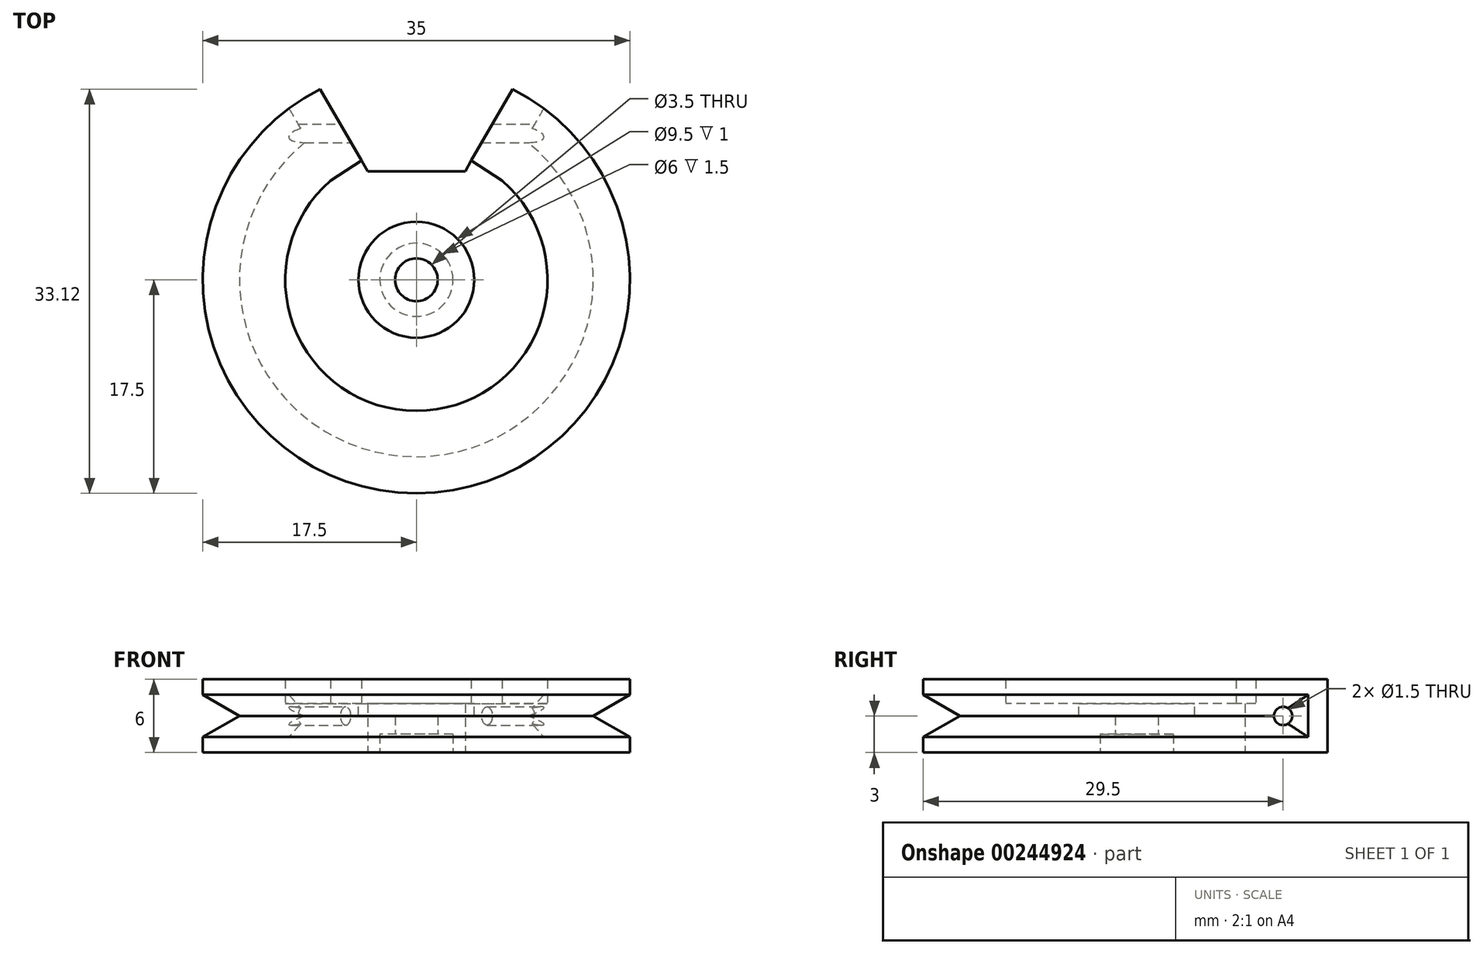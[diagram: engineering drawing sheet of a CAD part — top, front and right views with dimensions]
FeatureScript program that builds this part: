
annotation { "Feature Type Name" : "Feature", "Feature Type Description" : "" }
export const myFeature = defineFeature(function(context is Context, id is Id, definition is map)
    precondition{}
    {
        {
            var Q0;
            Q0=qCreatedBy(makeId("Top.planeOp"),FACE);
            var sketch = newSketch(context, id + "F0", { "sketchPlane" : qUnion([Q0])});
            skCircle(sketch, "E0", {"center": v(0, 0) * mm, "radius": 10.75 * mm});
            skCircle(sketch, "E1", {"center": v(0, 0) * mm, "radius": 17.5 * mm});
            skSolve(sketch);
        }
        {
            var Q0;
            Q0 = qSketchRegion(id + "F0", true);
            extrude(context, id + "F1", {"entities" : qUnion([Q0]), "depth" : 6 * mm});
        }
        {
            var Q0;
            Q0=qCreatedBy(makeId("Top.planeOp"),FACE);
            var sketch = newSketch(context, id + "F2", { "sketchPlane" : qUnion([Q0])});
            skCircle(sketch, "E2", {"center": v(0, 0) * mm, "radius": 10.75 * mm});
            skCircle(sketch, "E3", {"center": v(0, 0) * mm, "radius": 1.75 * mm});
            skSolve(sketch);
        }
        {
            var Q0;
            Q0 = qSketchRegion(id + "F2", true);
            extrude(context, id + "F3", {"entities" : qUnion([Q0]), "operationType" : NewBodyOperationType.ADD, "depth" : 4 * mm});
        }
        {
            var Q0;
            Q0=qCreatedBy(makeId("Front.planeOp"),FACE);
            var sketch = newSketch(context, id + "F4", { "sketchPlane" : qUnion([Q0])});
            skLineSegment(sketch, "E4", {"start": v(0, 0) * mm, "end": v(14.5, 0) * mm});
            skLineSegment(sketch, "E5", {"start": v(14.5, 0) * mm, "end": v(14.5, 3) * mm});
            skLineSegment(sketch, "E6", {"start": v(14.5, 3) * mm, "end": v(17.53, 4.75) * mm});
            skLineSegment(sketch, "E7", {"start": v(14.5, 3) * mm, "end": v(17.53, 1.25) * mm});
            skLineSegment(sketch, "E8", {"start": v(17.53, 1.25) * mm, "end": v(17.53, 4.75) * mm});
            skSolve(sketch);
        }
        {
            var Q0;
            Q0 = qSketchRegion(id + "F4", true);
            var Q1;
            Q1=makeQuery(id+"F1.opExtrude","CAP_EDGE",EDGE,{"disambiguationData":[OSD([sQuery(id+"F0.wireOp",EDGE,"E1")])],"isStart":false});
            sweep(context, id + "F5", {"operationType" : NewBodyOperationType.REMOVE, "profiles" : qUnion([Q0]), "path" : qUnion([Q1])});
        }
        {
            var Q0;
            Q0=qCreatedBy(makeId("Top.planeOp"),FACE);
            var sketch = newSketch(context, id + "F6", { "sketchPlane" : qUnion([Q0])});
            skArc(sketch, "E9", {"start": v(4, 8.9) * mm, "mid": v(0, 9.75) * mm, "end": v(-4, 8.9) * mm});
            skLineSegment(sketch, "E10", {"start": v(4, 8.9) * mm, "end": v(9.5, 18.42) * mm});
            skLineSegment(sketch, "E11", {"start": v(-4, 8.9) * mm, "end": v(-9.5, 18.42) * mm});
            skLineSegment(sketch, "E12", {"start": v(-9.5, 18.42) * mm, "end": v(9.5, 18.42) * mm});
            skLineSegment(sketch, "E13", {"start": v(-4, 8.9) * mm, "end": v(4, 8.9) * mm});
            skSolve(sketch);
        }
        {
            var Q0;
            Q0=qCreatedBy(makeId("Top.planeOp"),FACE);
            var sketch = newSketch(context, id + "F7", { "sketchPlane" : qUnion([Q0])});
            skArc(sketch, "E14", {"start": v(-7.89, 15.62) * mm, "mid": v(-9.2, 14.89) * mm, "end": v(-10.44, 14.05) * mm});
            skArc(sketch, "E15", {"start": v(7.03, 8.14) * mm, "mid": v(0, 10.75) * mm, "end": v(-7.03, 8.14) * mm});
            skLineSegment(sketch, "E16", {"start": v(-4.5, 9.76) * mm, "end": v(-7.89, 15.62) * mm});
            skLineSegment(sketch, "E17", {"start": v(4.5, 9.76) * mm, "end": v(7.89, 15.62) * mm});
            skLineSegment(sketch, "E18", {"start": v(-7.03, 8.14) * mm, "end": v(-10.44, 14.05) * mm});
            skLineSegment(sketch, "E19", {"start": v(7.03, 8.14) * mm, "end": v(10.44, 14.05) * mm});
            skLineSegment(sketch, "E20", {"start": v(5.94, 12.26) * mm, "end": v(8.54, 10.76) * mm});
            skLineSegment(sketch, "E21", {"start": v(-5.94, 12.26) * mm, "end": v(-8.54, 10.76) * mm});
            skLineSegment(sketch, "E22", {"start": v(7.03, 8.14) * mm, "end": v(4.5, 9.76) * mm});
            skPoint(sketch, "E23.orphan", {"position": v(4, 8.9) * mm});
            skLineSegment(sketch, "E24", {"start": v(-7.03, 8.14) * mm, "end": v(-4.5, 9.76) * mm});
            skPoint(sketch, "E25.orphan", {"position": v(-4, 8.9) * mm});
            skArc(sketch, "E26.trimOffspring", {"start": v(10.44, 14.05) * mm, "mid": v(9.2, 14.89) * mm, "end": v(7.89, 15.62) * mm});
            skSolve(sketch);
        }
        {
            var Q0;
            Q0 = qSketchRegion(id + "F6", true);
            extrude(context, id + "F8", {"entities" : qUnion([Q0]), "operationType" : NewBodyOperationType.REMOVE, "depth" : 6 * mm});
        }
        {
            var Q0;
            Q0 = qSketchRegion(id + "F7", true);
            extrude(context, id + "F9", {"entities" : qUnion([Q0]), "operationType" : NewBodyOperationType.ADD, "depth" : 6 * mm});
        }
        {
            var Q0;
            Q0=qCreatedBy(makeId("Right.planeOp"),FACE);
            var sketch = newSketch(context, id + "F10", { "sketchPlane" : qUnion([Q0])});
            skLineSegment(sketch, "E27", {"start": v(0, 0) * mm, "end": v(12, 0) * mm});
            skLineSegment(sketch, "E28", {"start": v(12, 0) * mm, "end": v(12, 3) * mm});
            skCircle(sketch, "E29", {"center": v(12, 3) * mm, "radius": 0.75 * mm});
            skSolve(sketch);
        }
        {
            var Q0;
            Q0=makeQuery(id+"F10.imprint","IMPRINT",FACE,{"disambiguationData":[TD([[makeQuery(id+"F10.imprint","IMPRINT",EDGE,{"derivedFrom":sQuery(id+"F10.wireOp",EDGE,"E29")}),1.0]])]});
            extrude(context, id + "F11", {"entities" : qUnion([Q0]), "operationType" : NewBodyOperationType.REMOVE, "endBound" : BoundingType.SYMMETRIC, "oppositeDirection" : true, "depth" : 100 * mm});
        }
        {
            var Q0;
            Q0=makeQuery(id+"F3.opExtrude","CAP_FACE",FACE,{"disambiguationData":[OSD([sQuery(id+"F2.wireOp",EDGE,"E2")])],"isStart":false});
            var sketch = newSketch(context, id + "F12", { "sketchPlane" : qUnion([Q0])});
            skCircle(sketch, "E30", {"center": v(0, 0) * mm, "radius": 4.75 * mm});
            skSolve(sketch);
        }
        {
            var Q0;
            Q0 = qSketchRegion(id + "F12", true);
            extrude(context, id + "F13", {"entities" : qUnion([Q0]), "operationType" : NewBodyOperationType.REMOVE, "oppositeDirection" : true, "depth" : 1 * mm});
        }
        {
            var Q0;
            Q0=qCreatedBy(makeId("Top.planeOp"),FACE);
            var sketch = newSketch(context, id + "F14", { "sketchPlane" : qUnion([Q0])});
            skCircle(sketch, "E31", {"center": v(0, 0) * mm, "radius": 3 * mm});
            skSolve(sketch);
        }
        {
            var Q0;
            Q0 = qSketchRegion(id + "F14", true);
            extrude(context, id + "F15", {"entities" : qUnion([Q0]), "operationType" : NewBodyOperationType.REMOVE, "depth" : 1.5 * mm});
        }
    });
